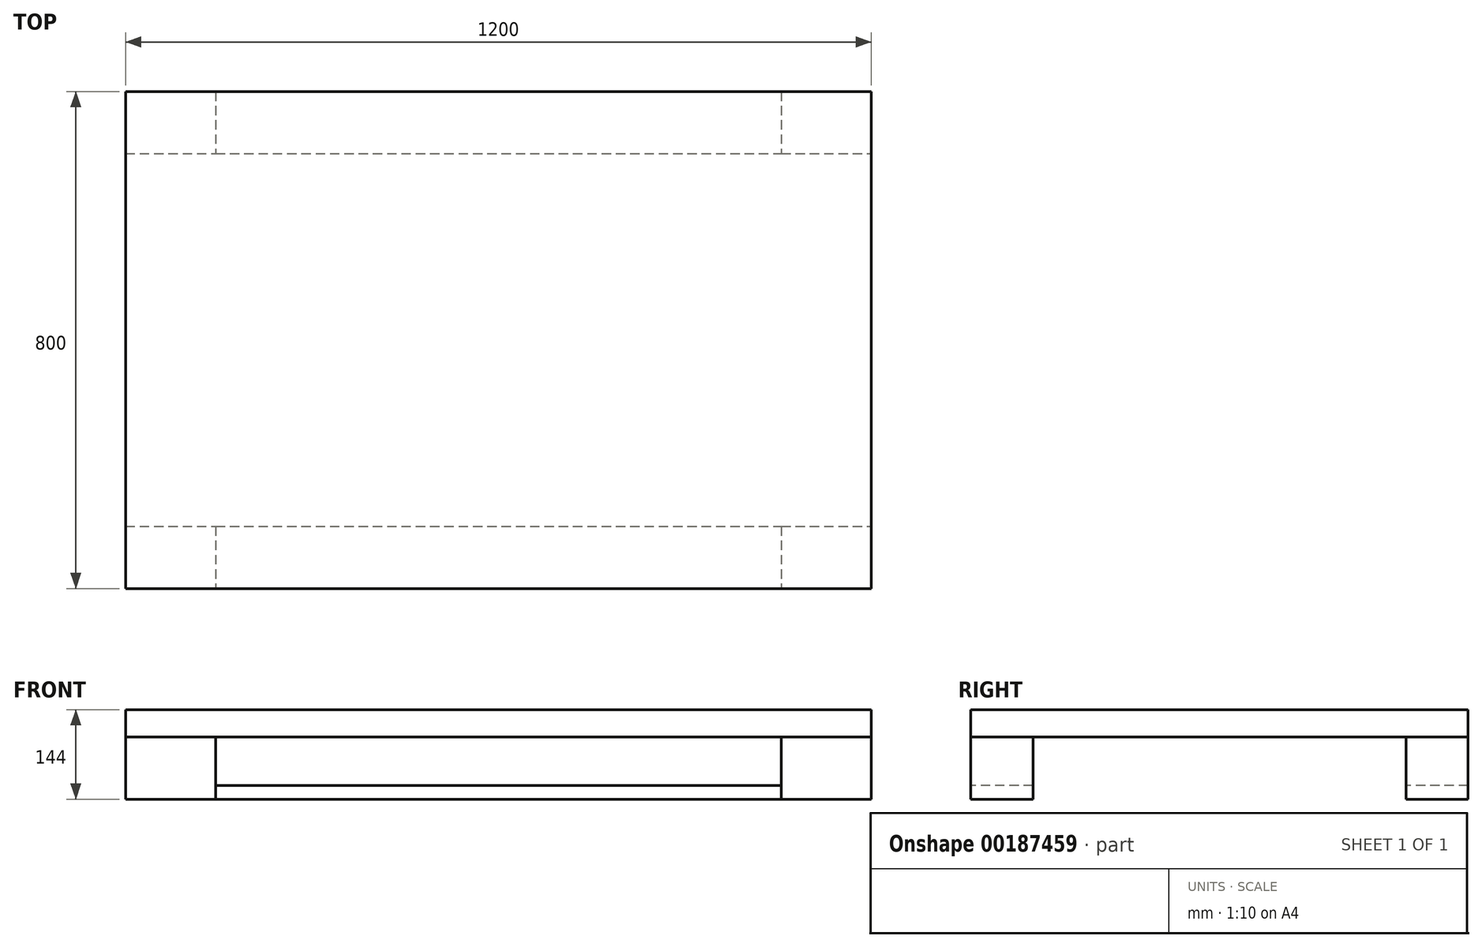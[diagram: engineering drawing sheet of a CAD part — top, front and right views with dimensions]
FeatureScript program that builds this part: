
annotation { "Feature Type Name" : "Feature", "Feature Type Description" : "" }
export const myFeature = defineFeature(function(context is Context, id is Id, definition is map)
    precondition{}
    {
        {
            var Q0;
            Q0=qCreatedBy(makeId("Top.planeOp"),FACE);
            var sketch = newSketch(context, id + "F0", { "sketchPlane" : qUnion([Q0])});
            skLineSegment(sketch, "E0.bottom", {"start": v(600, 400) * mm, "end": v(-600, 400) * mm});
            skLineSegment(sketch, "E0.top", {"start": v(600, -400) * mm, "end": v(-600, -400) * mm});
            skLineSegment(sketch, "E0.left", {"start": v(600, 400) * mm, "end": v(600, -400) * mm});
            skLineSegment(sketch, "E0.right", {"start": v(-600, 400) * mm, "end": v(-600, -400) * mm});
            skPoint(sketch, "E0.middle", {"position": v(0, 0) * mm});
            skLineSegment(sketch, "E1", {"start": v(-455, 400) * mm, "end": v(-455, -413.15) * mm});
            skLineSegment(sketch, "E2", {"start": v(-600, -300) * mm, "end": v(600, -300) * mm});
            skLineSegment(sketch, "E3", {"start": v(455, 400) * mm, "end": v(455, -400) * mm});
            skLineSegment(sketch, "E4", {"start": v(-600, 300) * mm, "end": v(600, 300) * mm});
            skSolve(sketch);
        }
        {
            var Q0;
            {var subQ0=sQuery(id+"F0.wireOp",EDGE,"E1");var subQ1=sQuery(id+"F0.wireOp",EDGE,"E0.bottom");var subQ2=makeQuery(id+"F0.imprint","INTERSECT",VERTEX,{"derivedFrom":[subQ1,subQ0]});Q0=makeQuery(id+"F0.imprint","IMPRINT",FACE,{"disambiguationData":[TD([[makeQuery(id+"F0.imprint","IMPRINT",EDGE,{"disambiguationData":[TD([[subQ2,1.0]])],"derivedFrom":subQ1}),1.0]])]});}
            var Q1;
            {var subQ0=sQuery(id+"F0.wireOp",EDGE,"E3");var subQ1=sQuery(id+"F0.wireOp",EDGE,"E0.top");var subQ2=makeQuery(id+"F0.imprint","INTERSECT",VERTEX,{"derivedFrom":[subQ1,subQ0]});Q1=makeQuery(id+"F0.imprint","IMPRINT",FACE,{"disambiguationData":[TD([[makeQuery(id+"F0.imprint","IMPRINT",EDGE,{"disambiguationData":[TD([[subQ2,-1.0]])],"derivedFrom":subQ1}),-1.0]])]});}
            extrude(context, id + "F1", {"entities" : qUnion([Q0, Q1]), "depth" : 22 * mm});
        }
        {
            var Q0;
            {var subQ0=sQuery(id+"F0.wireOp",EDGE,"E0.left");var subQ1=sQuery(id+"F0.wireOp",EDGE,"E0.top");var subQ2=makeQuery(id+"F0.imprint","INTERSECT",VERTEX,{"derivedFrom":[subQ1,subQ0]});Q0=makeQuery(id+"F0.imprint","IMPRINT",FACE,{"disambiguationData":[TD([[makeQuery(id+"F0.imprint","IMPRINT",EDGE,{"disambiguationData":[TD([[subQ2,-1.0]])],"derivedFrom":subQ1}),-1.0]])]});}
            var Q1;
            {var subQ0=sQuery(id+"F0.wireOp",EDGE,"E0.right");var subQ1=sQuery(id+"F0.wireOp",EDGE,"E0.top");var subQ2=makeQuery(id+"F0.imprint","INTERSECT",VERTEX,{"derivedFrom":[subQ1,subQ0]});Q1=makeQuery(id+"F0.imprint","IMPRINT",FACE,{"disambiguationData":[TD([[makeQuery(id+"F0.imprint","IMPRINT",EDGE,{"disambiguationData":[TD([[subQ2,1.0]])],"derivedFrom":subQ1}),-1.0]])]});}
            var Q2;
            {var subQ0=sQuery(id+"F0.wireOp",EDGE,"E0.right");var subQ1=sQuery(id+"F0.wireOp",EDGE,"E0.bottom");var subQ2=makeQuery(id+"F0.imprint","INTERSECT",VERTEX,{"derivedFrom":[subQ1,subQ0]});Q2=makeQuery(id+"F0.imprint","IMPRINT",FACE,{"disambiguationData":[TD([[makeQuery(id+"F0.imprint","IMPRINT",EDGE,{"disambiguationData":[TD([[subQ2,1.0]])],"derivedFrom":subQ1}),1.0]])]});}
            var Q3;
            {var subQ0=sQuery(id+"F0.wireOp",EDGE,"E0.left");var subQ1=sQuery(id+"F0.wireOp",EDGE,"E0.bottom");var subQ2=makeQuery(id+"F0.imprint","INTERSECT",VERTEX,{"derivedFrom":[subQ1,subQ0]});Q3=makeQuery(id+"F0.imprint","IMPRINT",FACE,{"disambiguationData":[TD([[makeQuery(id+"F0.imprint","IMPRINT",EDGE,{"disambiguationData":[TD([[subQ2,-1.0]])],"derivedFrom":subQ1}),1.0]])]});}
            extrude(context, id + "F2", {"entities" : qUnion([Q0, Q1, Q2, Q3]), "depth" : 100 * mm});
        }
        {
            var Q0;
            Q0=makeQuery(id+"F2.opExtrude","CAP_FACE",FACE,{"disambiguationData":[OSD([sQuery(id+"F0.wireOp",EDGE,"E0.top"),sQuery(id+"F0.wireOp",EDGE,"E0.left"),sQuery(id+"F0.wireOp",EDGE,"E2"),sQuery(id+"F0.wireOp",EDGE,"E3")])],"isStart":false});
            var sketch = newSketch(context, id + "F3", { "sketchPlane" : qUnion([Q0])});
            skLineSegment(sketch, "E5.bottom", {"start": v(600, -400) * mm, "end": v(-600, -400) * mm});
            skLineSegment(sketch, "E5.top", {"start": v(600, 400) * mm, "end": v(-600, 400) * mm});
            skLineSegment(sketch, "E5.left", {"start": v(600, -400) * mm, "end": v(600, 400) * mm});
            skLineSegment(sketch, "E5.right", {"start": v(-600, -400) * mm, "end": v(-600, 400) * mm});
            skSolve(sketch);
        }
        {
            var Q0;
            Q0 = qSketchRegion(id + "F3", true);
            extrude(context, id + "F4", {"entities" : qUnion([Q0]), "depth" : 44 * mm});
        }
    });
